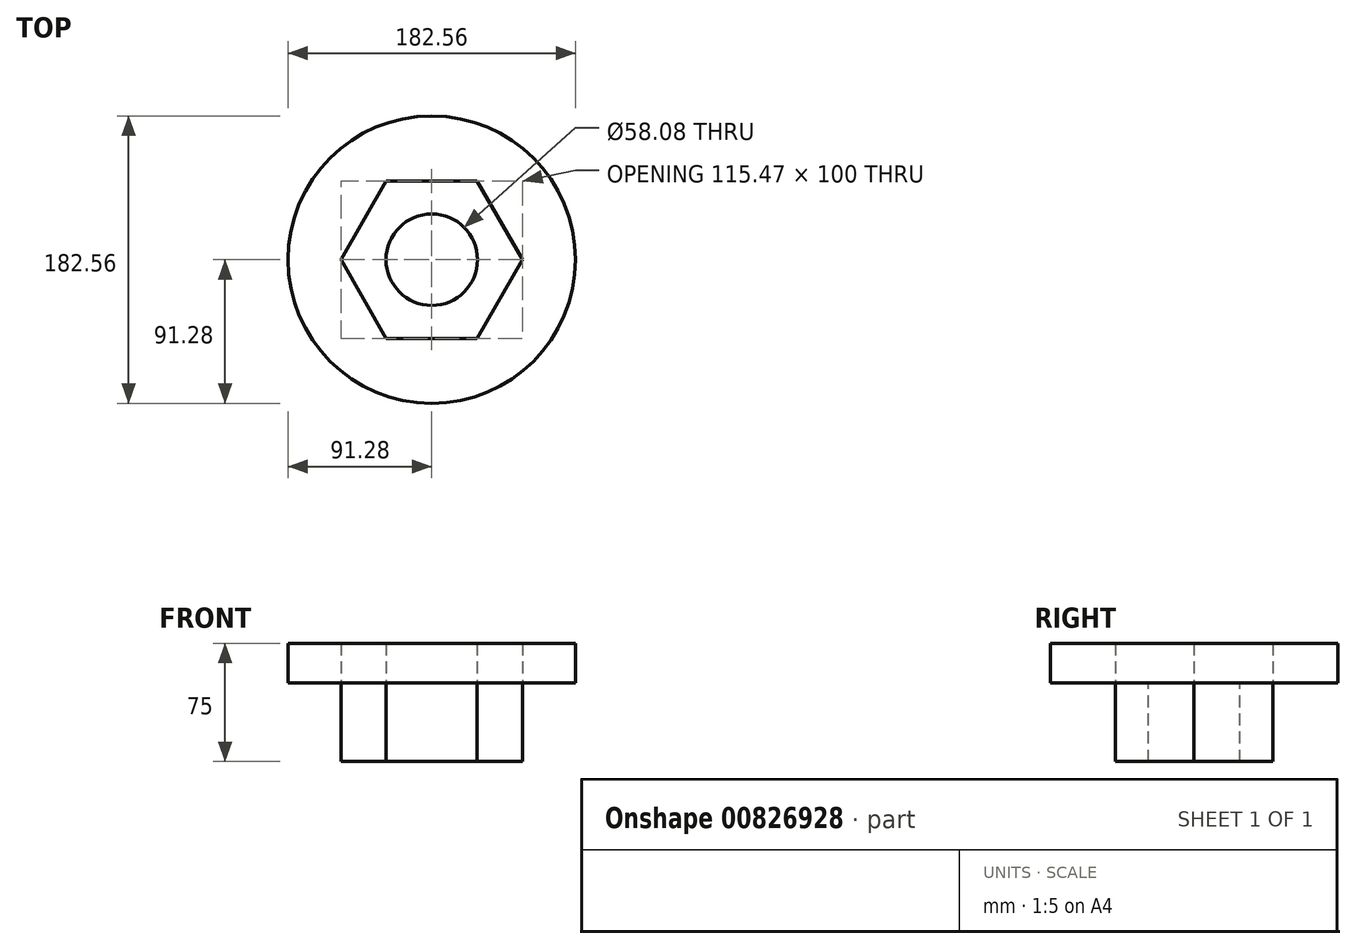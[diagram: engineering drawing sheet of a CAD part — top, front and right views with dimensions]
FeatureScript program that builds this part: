
annotation { "Feature Type Name" : "Feature", "Feature Type Description" : "" }
export const myFeature = defineFeature(function(context is Context, id is Id, definition is map)
    precondition{}
    {
        {
            var Q0;
            Q0=qCreatedBy(makeId("Top.planeOp"),FACE);
            var sketch = newSketch(context, id + "F0", { "sketchPlane" : qUnion([Q0])});
            skCircle(sketch, "E0.cCircle", {"center": v(0, 0) * mm, "radius": 50 * mm, "construction": true});
            skLineSegment(sketch, "E0.0", {"start": v(-28.87, 50) * mm, "end": v(28.87, 50) * mm});
            skLineSegment(sketch, "E0.1", {"start": v(28.87, 50) * mm, "end": v(57.74, 0) * mm});
            skLineSegment(sketch, "E0.2", {"start": v(57.74, 0) * mm, "end": v(28.87, -50) * mm});
            skLineSegment(sketch, "E0.3", {"start": v(28.87, -50) * mm, "end": v(-28.87, -50) * mm});
            skLineSegment(sketch, "E0.4", {"start": v(-28.87, -50) * mm, "end": v(-57.74, 0) * mm});
            skLineSegment(sketch, "E0.5", {"start": v(-57.74, 0) * mm, "end": v(-28.87, 50) * mm});
            skPoint(sketch, "E0.0.midPoint", {"position": v(0, 50) * mm});
            skSolve(sketch);
        }
        {
            var Q0;
            Q0=makeQuery(id+"F0.imprint","IMPRINT",FACE,{"disambiguationData":[TD([[makeQuery(id+"F0.imprint","IMPRINT",EDGE,{"derivedFrom":sQuery(id+"F0.wireOp",EDGE,"E0.0")}),-1.0]])]});
            extrude(context, id + "F1", {"entities" : qUnion([Q0]), "depth" : 50 * mm, "offsetDistance" : 25 * mm});
        }
        {
            var Q0;
            Q0=makeQuery(id+"F1.opExtrude","CAP_FACE",FACE,{"disambiguationData":[OSD([sQuery(id+"F0.wireOp",EDGE,"E0.0"),sQuery(id+"F0.wireOp",EDGE,"E0.1"),sQuery(id+"F0.wireOp",EDGE,"E0.2"),sQuery(id+"F0.wireOp",EDGE,"E0.3"),sQuery(id+"F0.wireOp",EDGE,"E0.4"),sQuery(id+"F0.wireOp",EDGE,"E0.5")])],"isStart":false});
            var sketch = newSketch(context, id + "F2", { "sketchPlane" : qUnion([Q0])});
            skCircle(sketch, "E1", {"center": v(0, 0) * mm, "radius": 29.04 * mm});
            skSolve(sketch);
        }
        {
            var Q0;
            Q0=makeQuery(id+"F2.imprint","IMPRINT",FACE,{"disambiguationData":[TD([[makeQuery(id+"F2.imprint","IMPRINT",EDGE,{"derivedFrom":sQuery(id+"F2.wireOp",EDGE,"E1")}),1.0]])]});
            extrude(context, id + "F3", {"entities" : qUnion([Q0]), "operationType" : NewBodyOperationType.REMOVE, "endBound" : BoundingType.UP_TO_NEXT, "oppositeDirection" : true, "depth" : 25 * mm, "offsetDistance" : 25 * mm});
        }
        {
            var Q0;
            Q0=makeQuery(id+"F1.opExtrude","CAP_FACE",FACE,{"disambiguationData":[OSD([sQuery(id+"F0.wireOp",EDGE,"E0.0"),sQuery(id+"F0.wireOp",EDGE,"E0.1"),sQuery(id+"F0.wireOp",EDGE,"E0.2"),sQuery(id+"F0.wireOp",EDGE,"E0.3"),sQuery(id+"F0.wireOp",EDGE,"E0.4"),sQuery(id+"F0.wireOp",EDGE,"E0.5")])],"isStart":false});
            var sketch = newSketch(context, id + "F4", { "sketchPlane" : qUnion([Q0])});
            skCircle(sketch, "E2", {"center": v(0, 0) * mm, "radius": 91.28 * mm});
            skSolve(sketch);
        }
        {
            var Q0;
            Q0=makeQuery(id+"F4.imprint","IMPRINT",FACE,{"disambiguationData":[TD([[makeQuery(id+"F4.imprint","IMPRINT",EDGE,{"derivedFrom":sQuery(id+"F4.wireOp",EDGE,"E2")}),1.0]])]});
            extrude(context, id + "F5", {"entities" : qUnion([Q0]), "depth" : 25 * mm, "offsetDistance" : 25 * mm});
        }
    });
